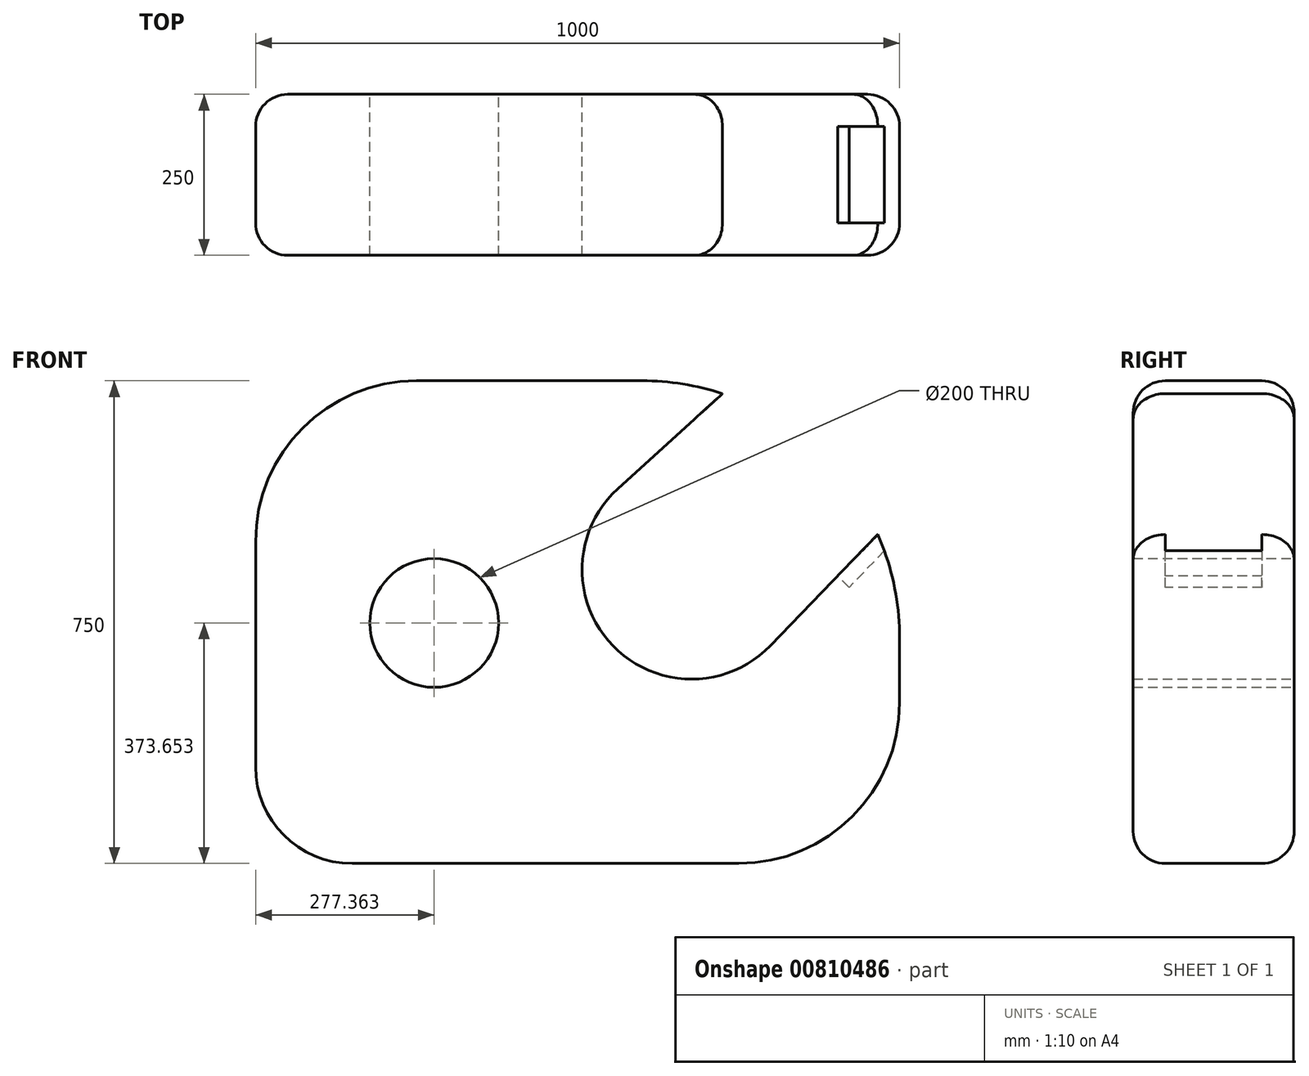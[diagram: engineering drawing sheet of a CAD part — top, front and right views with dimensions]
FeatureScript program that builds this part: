
annotation { "Feature Type Name" : "Feature", "Feature Type Description" : "" }
export const myFeature = defineFeature(function(context is Context, id is Id, definition is map)
    precondition{}
    {
        {
            var Q0;
            Q0=qCreatedBy(makeId("Front.planeOp"),FACE);
            var sketch = newSketch(context, id + "F0", { "sketchPlane" : qUnion([Q0])});
            skLineSegment(sketch, "E0.bottom", {"start": v(-677.4, 864.44) * mm, "end": v(-327.4, 864.44) * mm});
            skLineSegment(sketch, "E0.top", {"start": v(-777.4, 114.44) * mm, "end": v(-177.4, 114.44) * mm});
            skLineSegment(sketch, "E0.left", {"start": v(-927.4, 614.44) * mm, "end": v(-927.4, 264.44) * mm});
            skLineSegment(sketch, "E0.right", {"start": v(72.6, 464.44) * mm, "end": v(72.6, 364.44) * mm});
            skPoint(sketch, "E1.visualSharp", {"position": v(-927.4, 864.44) * mm});
            skArc(sketch, "E1.filletArc", {"start": v(-677.4, 864.44) * mm, "mid": v(-854.19, 791.22) * mm, "end": v(-927.4, 614.44) * mm});
            skPoint(sketch, "E2.visualSharp", {"position": v(-927.4, 114.44) * mm});
            skArc(sketch, "E2.filletArc", {"start": v(-927.4, 264.44) * mm, "mid": v(-883.48, 158.38) * mm, "end": v(-777.4, 114.44) * mm});
            skPoint(sketch, "E3.visualSharp", {"position": v(72.6, 114.44) * mm});
            skArc(sketch, "E3.filletArc", {"start": v(-177.4, 114.44) * mm, "mid": v(-0.63, 187.67) * mm, "end": v(72.6, 364.44) * mm});
            skPoint(sketch, "E4.visualSharp", {"position": v(72.6, 864.44) * mm});
            skArc(sketch, "E4.filletArc", {"start": v(72.6, 464.44) * mm, "mid": v(64.02, 546.79) * mm, "end": v(38.68, 625.6) * mm});
            skArc(sketch, "E5", {"start": v(-364.86, 696.61) * mm, "mid": v(-372.39, 452.46) * mm, "end": v(-128.12, 452.82) * mm});
            skLineSegment(sketch, "E6", {"start": v(-364.86, 696.61) * mm, "end": v(-202.46, 844.42) * mm});
            skLineSegment(sketch, "E7", {"start": v(-128.12, 452.82) * mm, "end": v(38.68, 625.6) * mm});
            skArc(sketch, "E8.trimOffspring", {"start": v(-202.46, 844.42) * mm, "mid": v(-264.14, 859.4) * mm, "end": v(-327.4, 864.44) * mm});
            skCircle(sketch, "E9", {"center": v(-650.05, 488.1) * mm, "radius": 100 * mm});
            skSolve(sketch);
        }
        {
            var Q0;
            Q0=makeQuery(id+"F0.imprint","IMPRINT",FACE,{"disambiguationData":[TD([[makeQuery(id+"F0.imprint","IMPRINT",EDGE,{"derivedFrom":sQuery(id+"F0.wireOp",EDGE,"E0.bottom")}),-1.0]])]});
            extrude(context, id + "F1", {"entities" : qUnion([Q0]), "depth" : 250 * mm, "offsetDistance" : 25 * mm});
        }
        {
            var Q0;
            Q0=makeQuery(id+"F1.opExtrude","CAP_EDGE",EDGE,{"disambiguationData":[OSD([sQuery(id+"F0.wireOp",EDGE,"E0.bottom")])],"isStart":false});
            var Q1;
            Q1=makeQuery(id+"F1.opExtrude","CAP_EDGE",EDGE,{"disambiguationData":[OSD([sQuery(id+"F0.wireOp",EDGE,"E0.bottom")])],"isStart":true});
            fillet(context, id + "F2", {"entities" : qUnion([Q0, Q1]), "radius" : 50 * mm, "tangentPropagation" : true, "allowEdgeOverflow" : false});
        }
        {
            var Q0;
            Q0=makeQuery(id+"F1.opExtrude","SWEPT_FACE",FACE,{"disambiguationData":[OSD([sQuery(id+"F0.wireOp",EDGE,"E7")])]});
            var sketch = newSketch(context, id + "F3", { "sketchPlane" : qUnion([Q0])});
            skLineSegment(sketch, "E10", {"start": v(200, 476.97) * mm, "end": v(50, 476.97) * mm});
            skLineSegment(sketch, "E11", {"start": v(50, 476.97) * mm, "end": v(50, 386.97) * mm});
            skLineSegment(sketch, "E12", {"start": v(50, 386.97) * mm, "end": v(200, 386.97) * mm});
            skLineSegment(sketch, "E13", {"start": v(200, 386.97) * mm, "end": v(200, 476.97) * mm});
            skSolve(sketch);
        }
        {
            var Q0;
            Q0=makeQuery(id+"F3.imprint","IMPRINT",FACE,{"disambiguationData":[TD([[makeQuery(id+"F3.imprint","IMPRINT",EDGE,{"derivedFrom":sQuery(id+"F3.wireOp",EDGE,"E10")}),1.0]])]});
            extrude(context, id + "F4", {"entities" : qUnion([Q0]), "operationType" : NewBodyOperationType.REMOVE, "oppositeDirection" : true, "depth" : 25 * mm, "offsetDistance" : 25 * mm});
        }
    });
